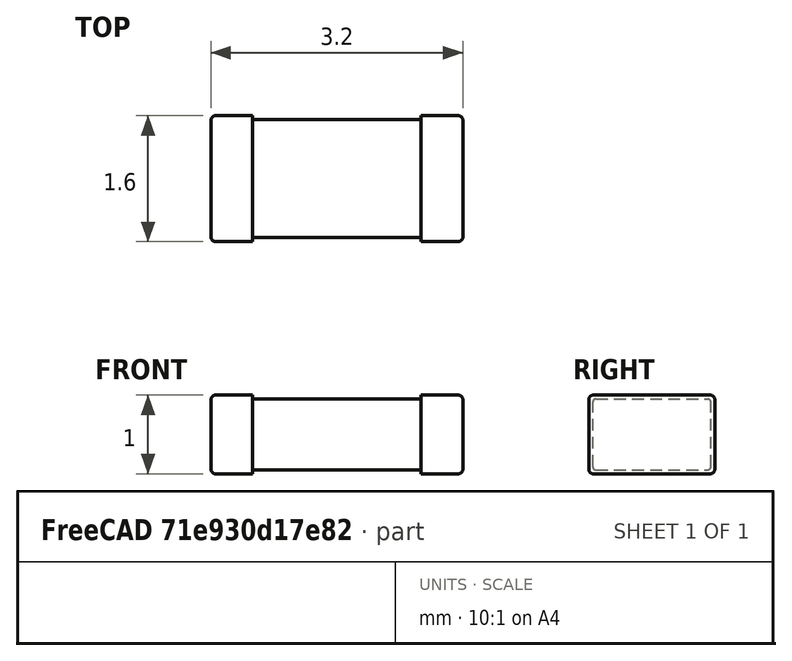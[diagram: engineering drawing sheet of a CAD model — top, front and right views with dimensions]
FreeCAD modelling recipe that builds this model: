
FCSTD DOCUMENT  (FreeCAD 0.16R6703 (Git))
Label: C_1206
License: All rights reserved
LicenseURL: http://en.wikipedia.org/wiki/All_rights_reserved
objects: Part::FeaturePython×4, Part::Box×2, Part::Fillet×2, Part::Mirroring×1, App::DocumentObjectGroup×1
note: 9 computed .brp shape members not serialized (recipe doc carries the construction recipe); baked Part::Feature solids carry a one-line shape summary decoded from their .brp

FEATURE [Part::Box] Box  label="Cube"
  Height = 0.9
  Length = 2.14
  Placement = pos=(-0.5,-0.38,0.02) rot=(0,0,1;0rad)
  Width = 1.5
FEATURE [Part::Fillet] Fillet  label="body-src"
  Base = -> Box
  Edges = 4 edges r=0.04: [Edge9,Edge10,Edge11,Edge12]
FEATURE [Part::Box] Box001  label="side-src"
  Height = 1
  Length = 0.53
  Placement = pos=(-1.6,-0.8,0) rot=(0,0,1;0rad)
  Width = 1.6
FEATURE [Part::Fillet] Fillet001  label="left-side-src"
  Base = -> Box001
  Edges = 8 edges r=0.06: [Edge1,Edge2,Edge3,Edge4,Edge9,Edge10,Edge11,Edge12]
FEATURE [Part::FeaturePython] Clone001  label="left-side-2"  # Draft clone (typed FeaturePython)
  Objects = -> [Fillet001]
  Scale = (1,1,1)
FEATURE [Part::Mirroring] Part__Mirroring  label="right-side-src"
  Base = (0,0,0)
  Normal = (1,0,0)
  Source = -> Clone001
FEATURE [App::DocumentObjectGroup] Group  label="src"
  Group = -> [Fillet,Box001,Fillet001,Part__Mirroring]
FEATURE [Part::FeaturePython] Clone  label="body"  # Draft clone (typed FeaturePython)
  Objects = -> [Fillet]
  Placement = pos=(-0.57,-0.37,0.03) rot=(0,0,1;0rad)
  Scale = (1,1,1)
FEATURE [Part::FeaturePython] Clone003  label="right-side"  # Draft clone (typed FeaturePython)
  Objects = -> [Part__Mirroring]
  Scale = (1,1,1)
FEATURE [Part::FeaturePython] Clone004  label="left-side"  # Draft clone (typed FeaturePython)
  Objects = -> [Clone001]
  Scale = (1,1,1)
